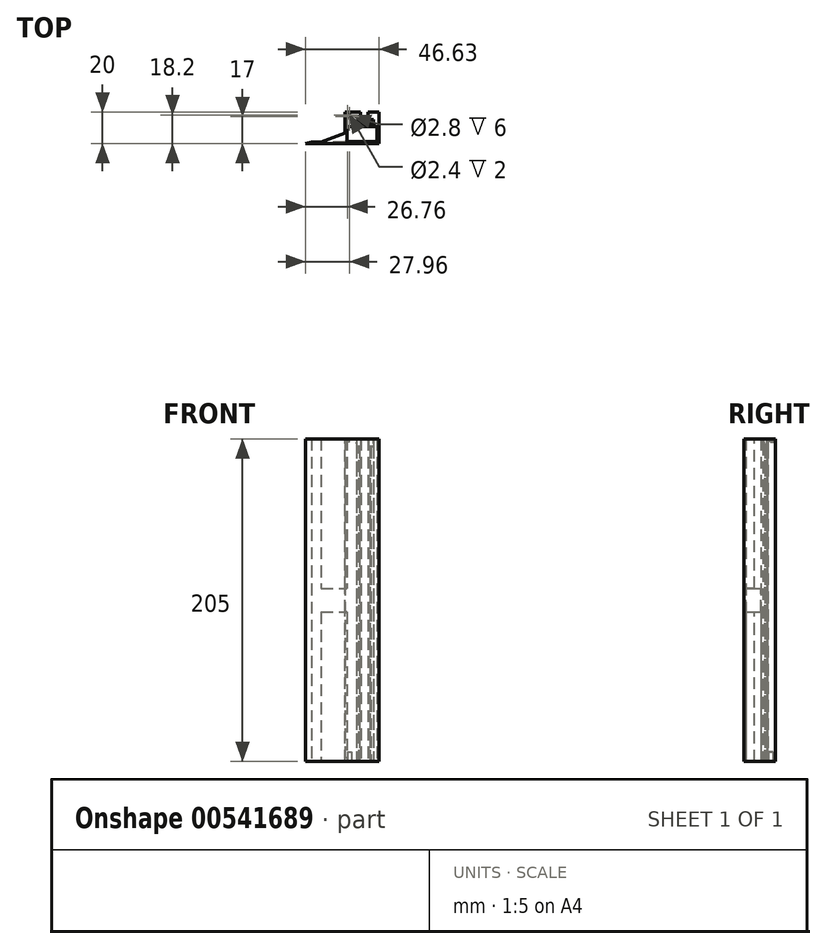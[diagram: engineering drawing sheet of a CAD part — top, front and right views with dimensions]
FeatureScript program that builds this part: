
annotation { "Feature Type Name" : "Feature", "Feature Type Description" : "" }
export const myFeature = defineFeature(function(context is Context, id is Id, definition is map)
    precondition{}
    {
        {
            var Q0;
            Q0=qCreatedBy(makeId("Top.planeOp"),FACE);
            var sketch = newSketch(context, id + "F0", { "sketchPlane" : qUnion([Q0])});
            skLineSegment(sketch, "E0", {"start": v(0, 0) * mm, "end": v(0, 8) * mm});
            skLineSegment(sketch, "E1", {"start": v(0, 8) * mm, "end": v(10, 8) * mm});
            skLineSegment(sketch, "E2", {"start": v(10, 8) * mm, "end": v(10.56, 1.62) * mm});
            skLineSegment(sketch, "E3", {"start": v(10.56, 1.62) * mm, "end": v(15.2, 2.02) * mm, "construction": true});
            skLineSegment(sketch, "E4", {"start": v(15.2, 2.02) * mm, "end": v(14.67, 8) * mm});
            skLineSegment(sketch, "E5", {"start": v(14.67, 8) * mm, "end": v(21.67, 8) * mm});
            skLineSegment(sketch, "E6", {"start": v(21.67, 8) * mm, "end": v(21.67, 0) * mm});
            skLineSegment(sketch, "E7", {"start": v(10.56, 1.62) * mm, "end": v(7.5, 1.35) * mm});
            skLineSegment(sketch, "E8", {"start": v(7.5, 1.35) * mm, "end": v(7.6, 0.05) * mm});
            skLineSegment(sketch, "E9", {"start": v(7.6, 0.05) * mm, "end": v(12.99, 0.53) * mm});
            skLineSegment(sketch, "E10", {"start": v(12.99, 0.53) * mm, "end": v(12.87, 1.82) * mm, "construction": true});
            skLineSegment(sketch, "E11.MirrorCS", {"start": v(15.2, 2.02) * mm, "end": v(18.25, 2.3) * mm});
            skLineSegment(sketch, "E12.MirrorCS", {"start": v(18.25, 2.3) * mm, "end": v(18.37, 1) * mm});
            skLineSegment(sketch, "E13.MirrorCS", {"start": v(18.37, 1) * mm, "end": v(12.99, 0.53) * mm});
            skLineSegment(sketch, "E14", {"start": v(10.46, 2.71) * mm, "end": v(9.4, 2.62) * mm});
            skLineSegment(sketch, "E15", {"start": v(9.4, 2.62) * mm, "end": v(9.49, 1.52) * mm});
            skLineSegment(sketch, "E16.MirrorCS", {"start": v(15.1, 3.12) * mm, "end": v(16.17, 3.21) * mm});
            skLineSegment(sketch, "E17.MirrorCS", {"start": v(16.17, 3.21) * mm, "end": v(16.26, 2.12) * mm});
            skLineSegment(sketch, "E18", {"start": v(0, 0) * mm, "end": v(0, -12) * mm});
            skLineSegment(sketch, "E19", {"start": v(0, -12) * mm, "end": v(21.67, -12) * mm});
            skLineSegment(sketch, "E20", {"start": v(21.67, -12) * mm, "end": v(21.67, 0) * mm});
            skLineSegment(sketch, "E21.bottom", {"start": v(1.33, -1.3) * mm, "end": v(20.33, -1.3) * mm});
            skLineSegment(sketch, "E21.top", {"start": v(1.33, -10.8) * mm, "end": v(20.33, -10.8) * mm});
            skLineSegment(sketch, "E21.left", {"start": v(1.33, -1.3) * mm, "end": v(1.33, -10.8) * mm});
            skLineSegment(sketch, "E21.right", {"start": v(20.33, -1.3) * mm, "end": v(20.33, -10.8) * mm});
            skLineSegment(sketch, "E22", {"start": v(10.83, -10.8) * mm, "end": v(10.83, -12) * mm, "construction": true});
            skSolve(sketch);
        }
        {
            var Q0;
            Q0=makeQuery(id+"F0.imprint","IMPRINT",FACE,{"disambiguationData":[TD([[makeQuery(id+"F0.imprint","IMPRINT",EDGE,{"derivedFrom":sQuery(id+"F0.wireOp",EDGE,"E0")}),-1.0]])]});
            extrude(context, id + "F1", {"entities" : qUnion([Q0]), "depth" : 204 * mm, "offsetDistance" : 25 * mm});
        }
        {
            var Q0;
            Q0=makeQuery(id+"F1.opExtrude","CAP_FACE",FACE,{"disambiguationData":[OSD([sQuery(id+"F0.wireOp",EDGE,"E0"),sQuery(id+"F0.wireOp",EDGE,"E1"),sQuery(id+"F0.wireOp",EDGE,"E2"),sQuery(id+"F0.wireOp",EDGE,"E4"),sQuery(id+"F0.wireOp",EDGE,"E5"),sQuery(id+"F0.wireOp",EDGE,"E6"),sQuery(id+"F0.wireOp",EDGE,"dtx2d9Iu-zEsN-xsry-goHi-OfcLoc71HTJ9"),sQuery(id+"F0.wireOp",EDGE,"E7"),sQuery(id+"F0.wireOp",EDGE,"E8"),sQuery(id+"F0.wireOp",EDGE,"E9"),sQuery(id+"F0.wireOp",EDGE,"E11.MirrorCS"),sQuery(id+"F0.wireOp",EDGE,"E12.MirrorCS"),sQuery(id+"F0.wireOp",EDGE,"E13.MirrorCS"),sQuery(id+"F0.wireOp",EDGE,"E14"),sQuery(id+"F0.wireOp",EDGE,"E15"),sQuery(id+"F0.wireOp",EDGE,"E16.MirrorCS"),sQuery(id+"F0.wireOp",EDGE,"E17.MirrorCS")])],"isStart":false});
            var sketch = newSketch(context, id + "F2", { "sketchPlane" : qUnion([Q0])});
            skLineSegment(sketch, "E23.0.0", {"start": v(14.67, 8) * mm, "end": v(15.1, 3.12) * mm, "construction": true});
            skLineSegment(sketch, "E23.0.1", {"start": v(15.1, 3.12) * mm, "end": v(16.17, 3.21) * mm});
            skLineSegment(sketch, "E23.0.2", {"start": v(16.17, 3.21) * mm, "end": v(16.26, 2.12) * mm});
            skLineSegment(sketch, "E23.0.3", {"start": v(16.26, 2.12) * mm, "end": v(18.25, 2.3) * mm});
            skLineSegment(sketch, "E23.0.4", {"start": v(18.25, 2.3) * mm, "end": v(18.37, 1) * mm});
            skLineSegment(sketch, "E23.0.5", {"start": v(18.37, 1) * mm, "end": v(7.6, 0.05) * mm});
            skLineSegment(sketch, "E23.0.6", {"start": v(7.6, 0.05) * mm, "end": v(7.5, 1.35) * mm});
            skLineSegment(sketch, "E23.0.7", {"start": v(7.5, 1.35) * mm, "end": v(9.49, 1.52) * mm});
            skLineSegment(sketch, "E23.0.8", {"start": v(9.49, 1.52) * mm, "end": v(9.4, 2.62) * mm});
            skLineSegment(sketch, "E23.0.9", {"start": v(9.4, 2.62) * mm, "end": v(10.46, 2.71) * mm});
            skLineSegment(sketch, "E23.0.10", {"start": v(10.46, 2.71) * mm, "end": v(10, 8) * mm, "construction": true});
            skLineSegment(sketch, "E23.0.11", {"start": v(10, 8) * mm, "end": v(0, 8) * mm});
            skLineSegment(sketch, "E23.0.12", {"start": v(0, 8) * mm, "end": v(0, 8) * mm});
            skLineSegment(sketch, "E23.0.13", {"start": v(0, 8) * mm, "end": v(21.67, 8) * mm});
            skLineSegment(sketch, "E23.0.14", {"start": v(21.67, 8) * mm, "end": v(21.67, 8) * mm});
            skLineSegment(sketch, "E23.0.15", {"start": v(21.67, 8) * mm, "end": v(14.67, 8) * mm});
            skLineSegment(sketch, "E24", {"start": v(10, 8) * mm, "end": v(14.67, 8) * mm});
            skLineSegment(sketch, "E25", {"start": v(15.1, 3.12) * mm, "end": v(10.46, 2.71) * mm});
            skLineSegment(sketch, "E26", {"start": v(12.78, 2.92) * mm, "end": v(12.99, 0.53) * mm, "construction": true});
            skLineSegment(sketch, "E27", {"start": v(7.5, 1.35) * mm, "end": v(7.4, 2.45) * mm});
            skLineSegment(sketch, "E28", {"start": v(7.4, 2.45) * mm, "end": v(9.4, 2.62) * mm});
            skLineSegment(sketch, "E29.MirrorCS", {"start": v(18.16, 3.39) * mm, "end": v(16.17, 3.21) * mm});
            skLineSegment(sketch, "E30.MirrorCS", {"start": v(18.25, 2.3) * mm, "end": v(18.16, 3.39) * mm});
            skSolve(sketch);
        }
        {
            var Q0;
            Q0=makeQuery(id+"F2.imprint","IMPRINT",FACE,{"disambiguationData":[TD([[makeQuery(id+"F2.imprint","IMPRINT",EDGE,{"derivedFrom":sQuery(id+"F2.wireOp",EDGE,"E23.0.1")}),1.0]])]});
            var Q1;
            Q1=makeQuery(id+"F2.imprint","IMPRINT",FACE,{"disambiguationData":[TD([[makeQuery(id+"F2.imprint","IMPRINT",EDGE,{"derivedFrom":sQuery(id+"F2.wireOp",EDGE,"E24")}),-1.0]])]});
            extrude(context, id + "F3", {"entities" : qUnion([Q0, Q1]), "operationType" : NewBodyOperationType.ADD, "depth" : 1 * mm, "offsetDistance" : 25 * mm});
        }
        {
            var Q0;
            {var subQ0=sQuery(id+"F0.wireOp",EDGE,"E15");var subQ1=sQuery(id+"F0.wireOp",EDGE,"E8");var subQ2=sQuery(id+"F0.wireOp",EDGE,"E14");var subQ3=sQuery(id+"F0.wireOp",EDGE,"E7");var subQ4=sQuery(id+"F0.wireOp",EDGE,"E16.MirrorCS");Q0=makeQuery(id+"F3.boolean.opBoolean","SPLIT",FACE,{"disambiguationData":[TD([makeQuery(id+"F1.opExtrude","SWEPT_FACE",FACE,{"disambiguationData":[OSD([subQ3])]})])],"derivedFrom":makeQuery(id+"F1.opExtrude","CAP_FACE",FACE,{"disambiguationData":[OSD([sQuery(id+"F0.wireOp",EDGE,"E0"),sQuery(id+"F0.wireOp",EDGE,"E1"),sQuery(id+"F0.wireOp",EDGE,"E2"),sQuery(id+"F0.wireOp",EDGE,"E4"),sQuery(id+"F0.wireOp",EDGE,"E5"),sQuery(id+"F0.wireOp",EDGE,"E6"),sQuery(id+"F0.wireOp",EDGE,"dtx2d9Iu-zEsN-xsry-goHi-OfcLoc71HTJ9"),subQ3,subQ1,sQuery(id+"F0.wireOp",EDGE,"E9"),sQuery(id+"F0.wireOp",EDGE,"E11.MirrorCS"),sQuery(id+"F0.wireOp",EDGE,"E12.MirrorCS"),sQuery(id+"F0.wireOp",EDGE,"E13.MirrorCS"),subQ2,subQ0,subQ4,sQuery(id+"F0.wireOp",EDGE,"E17.MirrorCS")])],"isStart":false})});}
            var sketch = newSketch(context, id + "F4", { "sketchPlane" : qUnion([Q0])});
            skLineSegment(sketch, "E31.0.0", {"start": v(9.49, 1.52) * mm, "end": v(9.4, 2.62) * mm});
            skLineSegment(sketch, "E31.0.1", {"start": v(9.4, 2.62) * mm, "end": v(7.4, 2.45) * mm});
            skLineSegment(sketch, "E31.0.2", {"start": v(7.4, 2.45) * mm, "end": v(7.5, 1.35) * mm});
            skLineSegment(sketch, "E31.0.3", {"start": v(7.5, 1.35) * mm, "end": v(9.49, 1.52) * mm});
            skLineSegment(sketch, "E32.0.0", {"start": v(18.25, 2.3) * mm, "end": v(18.16, 3.39) * mm});
            skLineSegment(sketch, "E32.0.1", {"start": v(18.16, 3.39) * mm, "end": v(16.17, 3.21) * mm});
            skLineSegment(sketch, "E32.0.2", {"start": v(16.17, 3.21) * mm, "end": v(16.26, 2.12) * mm});
            skLineSegment(sketch, "E32.0.3", {"start": v(16.26, 2.12) * mm, "end": v(18.25, 2.3) * mm});
            skSolve(sketch);
        }
        {
            var Q0;
            Q0 = qSketchRegion(id + "F4", true);
            extrude(context, id + "F5", {"entities" : qUnion([Q0]), "operationType" : NewBodyOperationType.REMOVE, "oppositeDirection" : true, "depth" : 4 * mm, "offsetDistance" : 25 * mm});
        }
        {
            var Q0;
            Q0=makeQuery(id+"F1.opExtrude","SWEPT_EDGE",EDGE,{"disambiguationData":[OSD([sQuery(id+"F0.wireOp",EDGE,"E11.MirrorCS"),sQuery(id+"F0.wireOp",EDGE,"E17.MirrorCS")])]});
            var Q1;
            Q1=makeQuery(id+"F1.opExtrude","SWEPT_EDGE",EDGE,{"disambiguationData":[OSD([sQuery(id+"F0.wireOp",EDGE,"E7"),sQuery(id+"F0.wireOp",EDGE,"E15")])]});
            chamfer(context, id + "F6", {"entities" : qUnion([Q0, Q1]), "width" : .5 * mm, "tangentPropagation" : true});
        }
        {
            var Q0;
            Q0=makeQuery(id+"F1.opExtrude","CAP_FACE",FACE,{"disambiguationData":[OSD([sQuery(id+"F0.wireOp",EDGE,"E0"),sQuery(id+"F0.wireOp",EDGE,"E1"),sQuery(id+"F0.wireOp",EDGE,"E2"),sQuery(id+"F0.wireOp",EDGE,"E4"),sQuery(id+"F0.wireOp",EDGE,"E5"),sQuery(id+"F0.wireOp",EDGE,"E6"),sQuery(id+"F0.wireOp",EDGE,"dtx2d9Iu-zEsN-xsry-goHi-OfcLoc71HTJ9"),sQuery(id+"F0.wireOp",EDGE,"E7"),sQuery(id+"F0.wireOp",EDGE,"E8"),sQuery(id+"F0.wireOp",EDGE,"E9"),sQuery(id+"F0.wireOp",EDGE,"E11.MirrorCS"),sQuery(id+"F0.wireOp",EDGE,"E12.MirrorCS"),sQuery(id+"F0.wireOp",EDGE,"E13.MirrorCS"),sQuery(id+"F0.wireOp",EDGE,"E14"),sQuery(id+"F0.wireOp",EDGE,"E15"),sQuery(id+"F0.wireOp",EDGE,"E16.MirrorCS"),sQuery(id+"F0.wireOp",EDGE,"E17.MirrorCS")])],"isStart":true});
            var sketch = newSketch(context, id + "F7", { "sketchPlane" : qUnion([Q0])});
            skLineSegment(sketch, "E33", {"start": v(10, -8) * mm, "end": v(14.67, -8) * mm});
            skCircle(sketch, "E34", {"center": v(3, -5) * mm, "radius": 1.4 * mm});
            skSolve(sketch);
        }
        {
            var Q0;
            Q0=makeQuery(id+"F7.imprint","IMPRINT",FACE,{"disambiguationData":[TD([[makeQuery(id+"F7.imprint","IMPRINT",EDGE,{"derivedFrom":sQuery(id+"F7.wireOp",EDGE,"E34")}),1.0]])]});
            extrude(context, id + "F8", {"entities" : qUnion([Q0]), "operationType" : NewBodyOperationType.REMOVE, "oppositeDirection" : true, "depth" : 6 * mm, "offsetDistance" : 25 * mm});
        }
        {
            var Q0;
            Q0=makeQuery(id+"F3.opExtrude","CAP_EDGE",EDGE,{"disambiguationData":[OSD([sQuery(id+"F2.wireOp",EDGE,"E23.0.5")])],"isStart":false});
            fillet(context, id + "F9", {"entities" : qUnion([Q0]), "radius" : 3 * mm, "tangentPropagation" : true, "allowEdgeOverflow" : false});
        }
        {
            var Q0;
            {var subQ0=sQuery(id+"F0.wireOp",EDGE,"E18");var subQ1=sQuery(id+"F0.wireOp",EDGE,"E0");Q0=makeQuery(id+"F8.boolean.opBoolean","MERGE",FACE,{"derivedFrom":[makeQuery(id+"F3.boolean.opBoolean","MERGE",FACE,{"derivedFrom":[makeQuery(id+"F1.opExtrude","SWEPT_FACE",FACE,{"disambiguationData":[OSD([subQ1,subQ0])]}),makeQuery(id+"F3.opExtrude","SWEPT_FACE",FACE,{"disambiguationData":[OSD([subQ1,subQ0])]})]}),makeQuery(id+"F8.opExtrude","SWEPT_FACE",FACE,{"disambiguationData":[OSD([subQ1,subQ0])]})]});}
            var sketch = newSketch(context, id + "F10", { "sketchPlane" : qUnion([Q0])});
            skLineSegment(sketch, "E35.0.0", {"start": v(1.3, 0) * mm, "end": v(10.8, 0) * mm, "construction": true});
            skLineSegment(sketch, "E35.0.1", {"start": v(10.8, 0) * mm, "end": v(10.8, 205) * mm, "construction": true});
            skLineSegment(sketch, "E35.0.2", {"start": v(10.8, 205) * mm, "end": v(1.3, 205) * mm, "construction": true});
            skLineSegment(sketch, "E35.0.3", {"start": v(1.3, 205) * mm, "end": v(1.3, 0) * mm, "construction": true});
            skLineSegment(sketch, "E36.bottom", {"start": v(10.8, 95) * mm, "end": v(1.3, 95) * mm});
            skLineSegment(sketch, "E36.top", {"start": v(10.8, 110) * mm, "end": v(1.3, 110) * mm});
            skLineSegment(sketch, "E36.left", {"start": v(10.8, 95) * mm, "end": v(10.8, 110) * mm});
            skLineSegment(sketch, "E36.right", {"start": v(1.3, 95) * mm, "end": v(1.3, 110) * mm});
            skSolve(sketch);
        }
        {
            var Q0;
            Q0 = qSketchRegion(id + "F10", true);
            extrude(context, id + "F11", {"entities" : qUnion([Q0]), "operationType" : NewBodyOperationType.REMOVE, "endBound" : BoundingType.UP_TO_NEXT, "oppositeDirection" : true, "depth" : 25 * mm, "offsetDistance" : 25 * mm});
        }
        {
            var Q0;
            Q0=makeQuery(id+"F3.opExtrude","CAP_FACE",FACE,{"disambiguationData":[OSD([sQuery(id+"F0.wireOp",EDGE,"E0"),sQuery(id+"F0.wireOp",EDGE,"E6"),sQuery(id+"F0.wireOp",EDGE,"E18"),sQuery(id+"F0.wireOp",EDGE,"E19"),sQuery(id+"F0.wireOp",EDGE,"E20"),sQuery(id+"F0.wireOp",EDGE,"E21.bottom"),sQuery(id+"F0.wireOp",EDGE,"E21.top"),sQuery(id+"F0.wireOp",EDGE,"E21.left"),sQuery(id+"F0.wireOp",EDGE,"E21.right"),sQuery(id+"F2.wireOp",EDGE,"E23.0.1"),sQuery(id+"F2.wireOp",EDGE,"E23.0.4"),sQuery(id+"F2.wireOp",EDGE,"E23.0.5"),sQuery(id+"F2.wireOp",EDGE,"E23.0.6"),sQuery(id+"F2.wireOp",EDGE,"E23.0.9"),sQuery(id+"F2.wireOp",EDGE,"E23.0.13"),sQuery(id+"F2.wireOp",EDGE,"E23.0.15"),sQuery(id+"F2.wireOp",EDGE,"E24"),sQuery(id+"F2.wireOp",EDGE,"E25"),sQuery(id+"F2.wireOp",EDGE,"E27"),sQuery(id+"F2.wireOp",EDGE,"E28"),sQuery(id+"F2.wireOp",EDGE,"E29.MirrorCS"),sQuery(id+"F2.wireOp",EDGE,"E30.MirrorCS")])],"isStart":false});
            var sketch = newSketch(context, id + "F12", { "sketchPlane" : qUnion([Q0])});
            skCircle(sketch, "E37", {"center": v(1.8, 6.2) * mm, "radius": 1.2 * mm});
            skSolve(sketch);
        }
        {
            var Q0;
            Q0 = qSketchRegion(id + "F12", true);
            extrude(context, id + "F13", {"entities" : qUnion([Q0]), "operationType" : NewBodyOperationType.REMOVE, "oppositeDirection" : true, "depth" : 2 * mm, "offsetDistance" : 25 * mm});
        }
        {
            var Q0;
            Q0=makeQuery(id+"F1.opExtrude","CAP_FACE",FACE,{"disambiguationData":[OSD([sQuery(id+"F0.wireOp",EDGE,"E0"),sQuery(id+"F0.wireOp",EDGE,"E1"),sQuery(id+"F0.wireOp",EDGE,"E2"),sQuery(id+"F0.wireOp",EDGE,"E4"),sQuery(id+"F0.wireOp",EDGE,"E5"),sQuery(id+"F0.wireOp",EDGE,"E6"),sQuery(id+"F0.wireOp",EDGE,"E7"),sQuery(id+"F0.wireOp",EDGE,"E8"),sQuery(id+"F0.wireOp",EDGE,"E9"),sQuery(id+"F0.wireOp",EDGE,"E11.MirrorCS"),sQuery(id+"F0.wireOp",EDGE,"E12.MirrorCS"),sQuery(id+"F0.wireOp",EDGE,"E13.MirrorCS"),sQuery(id+"F0.wireOp",EDGE,"E14"),sQuery(id+"F0.wireOp",EDGE,"E15"),sQuery(id+"F0.wireOp",EDGE,"E16.MirrorCS"),sQuery(id+"F0.wireOp",EDGE,"E17.MirrorCS"),sQuery(id+"F0.wireOp",EDGE,"E18"),sQuery(id+"F0.wireOp",EDGE,"E19"),sQuery(id+"F0.wireOp",EDGE,"E20"),sQuery(id+"F0.wireOp",EDGE,"E21.bottom"),sQuery(id+"F0.wireOp",EDGE,"E21.top"),sQuery(id+"F0.wireOp",EDGE,"E21.left"),sQuery(id+"F0.wireOp",EDGE,"E21.right")])],"isStart":true});
            var sketch = newSketch(context, id + "F14", { "sketchPlane" : qUnion([Q0])});
            skLineSegment(sketch, "E38", {"start": v(0.04, 12) * mm, "end": v(-24.96, 12) * mm});
            skLineSegment(sketch, "E39", {"start": v(-24.96, 12) * mm, "end": v(-21.05, 11.19) * mm});
            skLineSegment(sketch, "E40", {"start": v(-21.05, 11.19) * mm, "end": v(0.04, 10.8) * mm});
            skLineSegment(sketch, "E41", {"start": v(0.04, 10.8) * mm, "end": v(0.04, 12) * mm});
            skPoint(sketch, "E42.0", {"position": v(0, 10.8) * mm});
            skSolve(sketch);
        }
        {
            var Q0;
            Q0 = qSketchRegion(id + "F14", true);
            var Q1;
            Q1=makeQuery(id+"F3.opExtrude","CAP_FACE",FACE,{"disambiguationData":[OSD([sQuery(id+"F0.wireOp",EDGE,"E0"),sQuery(id+"F0.wireOp",EDGE,"E6"),sQuery(id+"F0.wireOp",EDGE,"E18"),sQuery(id+"F0.wireOp",EDGE,"E19"),sQuery(id+"F0.wireOp",EDGE,"E20"),sQuery(id+"F0.wireOp",EDGE,"E21.bottom"),sQuery(id+"F0.wireOp",EDGE,"E21.top"),sQuery(id+"F0.wireOp",EDGE,"E21.left"),sQuery(id+"F0.wireOp",EDGE,"E21.right"),sQuery(id+"F2.wireOp",EDGE,"E23.0.1"),sQuery(id+"F2.wireOp",EDGE,"E23.0.4"),sQuery(id+"F2.wireOp",EDGE,"E23.0.5"),sQuery(id+"F2.wireOp",EDGE,"E23.0.6"),sQuery(id+"F2.wireOp",EDGE,"E23.0.9"),sQuery(id+"F2.wireOp",EDGE,"E23.0.13"),sQuery(id+"F2.wireOp",EDGE,"E23.0.15"),sQuery(id+"F2.wireOp",EDGE,"E24"),sQuery(id+"F2.wireOp",EDGE,"E25"),sQuery(id+"F2.wireOp",EDGE,"E27"),sQuery(id+"F2.wireOp",EDGE,"E28"),sQuery(id+"F2.wireOp",EDGE,"E29.MirrorCS"),sQuery(id+"F2.wireOp",EDGE,"E30.MirrorCS")])],"isStart":false});
            extrude(context, id + "F15", {"entities" : qUnion([Q0]), "operationType" : NewBodyOperationType.ADD, "endBound" : BoundingType.UP_TO_SURFACE, "oppositeDirection" : true, "depth" : 25 * mm, "endBoundEntityFace" : qUnion([Q1]), "offsetDistance" : 25 * mm});
        }
        {
            var Q0;
            {var subQ0=sQuery(id+"F0.wireOp",EDGE,"E18");var subQ1=sQuery(id+"F0.wireOp",EDGE,"E0");Q0=makeQuery(id+"F15.boolean.opBoolean","INTERSECT",EDGE,{"disambiguationData":[OD(0.0)],"derivedFrom":[makeQuery(id+"F3.boolean.opBoolean","MERGE",FACE,{"derivedFrom":[makeQuery(id+"F1.opExtrude","SWEPT_FACE",FACE,{"disambiguationData":[OSD([subQ1,subQ0])]}),makeQuery(id+"F3.opExtrude","SWEPT_FACE",FACE,{"disambiguationData":[OSD([subQ1,subQ0])]})]}),makeQuery(id+"F15.opExtrude","SWEPT_FACE",FACE,{"disambiguationData":[OSD([sQuery(id+"F14.wireOp",EDGE,"E40")])]})]});}
            var Q1;
            {var subQ0=sQuery(id+"F0.wireOp",EDGE,"E18");var subQ1=sQuery(id+"F0.wireOp",EDGE,"E0");Q1=makeQuery(id+"F15.boolean.opBoolean","INTERSECT",EDGE,{"disambiguationData":[OD(1.0)],"derivedFrom":[makeQuery(id+"F3.boolean.opBoolean","MERGE",FACE,{"derivedFrom":[makeQuery(id+"F1.opExtrude","SWEPT_FACE",FACE,{"disambiguationData":[OSD([subQ1,subQ0])]}),makeQuery(id+"F3.opExtrude","SWEPT_FACE",FACE,{"disambiguationData":[OSD([subQ1,subQ0])]})]}),makeQuery(id+"F15.opExtrude","SWEPT_FACE",FACE,{"disambiguationData":[OSD([sQuery(id+"F14.wireOp",EDGE,"E40")])]})]});}
            chamfer(context, id + "F16", {"entities" : qUnion([Q0, Q1]), "chamferType" : ChamferType.OFFSET_ANGLE, "width" : 15 * mm, "oppositeDirection" : false, "angle" : 20 * degree, "tangentPropagation" : true});
        }
    });
